# Revit family: Camera-Security-Canon-Box
name_source: partatom
category: Security Devices
revit_build: Autodesk Revit MEP 2012 (Build: 20110916_2132(x64)
units: mm (PartAtom-declared; Revit-internal decimal feet)

## types (4) — shared parameters
Alarm Triggers = External Device Input, Intelligent Function (Video), Intelligent Function (Volume), Timer
Audio In = Φ3.5mm (Φ0.14 in.) Mini-Jack Connector (Monaural), Switch Line IN/MIC IN in the Setting Page. LINE IN x 1 (Connect to an Amplifier Microphone) or MIC IN x 1 (Connect to a Microphone w/o Amplifier)
Date Modified = September 15, 2014
Day and Night = Auto/Manual
Default Elevation = 48 "
Description = See Part Description
Equipment Abbreviation = SC
Family Version = 1.0
IPv4 Protocol = TCP/IP, UDP, HTTP, FTP, SNMP (MIB2), SMTP (Client), DHCP (Client), DNS (Client), ARP, ICMP, POP3, NTP, SMTP Authentication, RTSP, WV-HTTP (Canon Proprietary), ONVIF
Image Sensor = 1/3 type CMOS (Primary Color Filter)
Lens Type = Fixed
Manufacturer = Canon U.S.A., Inc.
Maximum Framerate = JPEG: 0.1 - 30 fps; H.263: 1/2/3/5/6/10/15/30 fps
Minimum Illumination = 0 lx
Model = See Part Number
Model Disclaimer = This 3D model is a simulation of a highly customizable piece of Canon equipment. For assistance in selecting the right Canon equipment for your project, please contact Canon U.S.A., Inc.
Operating Conditions = Temperature:  -10°C - +50°C (+14°F - +122°F); Humidity: 5% - 85% (Without Condensation)
Product Documentation Link = http://www.usa.canon.com
Product Page URL = http://www.usa.canon.com
Scanning System = Progressive
URL = http://www.usa.canon.com
zz Angle 11 = 90.000°
zz Length 10 = 5.118 "
zz Length 14 = -5.96 "
zz Length 19 = 2.28 "
zz Length 20 = 9.71 "
zz Length 23 = 6.529 "
zz Length 26 = 0.157 "
zz Length 28 = 0.736 "
zz Length 3 = 4 "
zz Length 32 = -1.153 "
zz Length 34 = 1.732 "
zz Length 38 = 2.632 "
zz Length 39 = 4.893 "
zz Length 4 = 0.5 "
zz Length 41 = -6.085 "
zz Length 43 = 1.153 "
zz Length 48 = 20 "
zz Length 52 = 2.305 "
zz Length 53 = 3.2 "
zz Length 55 = 0.5 "
zz Length 6 = 6.89 "
zz Length 62 = -1.153 "
zz Length 65 = 1.153 "
zz Length 66 = 8.742 "
zz Length 67 = 6.275 "
zz Length 69 = 6.15 "
zz Length 71 = -6.085 "
zz Length 73 = 1.125 "
zz Length 77 = 3.116 "
zz Length 79 = 6.275 "

## per-type parameters (varying)
| type | Angular Field of View | Effective Pixels | Height | Megapixels | Resolution | Shutter Speed | Width | zz Integer 2 | zz Length 31 | zz Length 36 | zz Length 9 |
| 2.1 MP, Micro | Horizontal: 96° (W) - 96° (T); Vertical: 60.5° (W) - 60.5° (T) | 2.1 Million Pixels | 1.25 " | 2.1 | JPEG, H.264: 1920x1080, 1280x920, 1280x720, 960x5440, 640x480, 640x360, 480x270, 320x240, 320x180 | 1, 1/2, 1/4, 1/8, 1/15, 1/30, 1/60, 1/100, 1/120, 1/250, 1/500, 1/1000, 1/2000, 1/4000, 1/8000, 1/10000, 1/16000 sec. | 2.125 " | 1 | 4.49 " | 2.125 " | 1.25 " |
| 2.1 MP, Standard | Horizontal: 112.6° (W) - 36.7° (T); Vertical: 60.8° (W) - 20.6° (T) | 2.1 Million Pixels | 3.15 " | 2.1 | JPEG, H.264: 1920x1080, 1280x920, 1280x720, 960x5440, 640x480, 640x360, 480x270, 320x240, 320x180 | 1, 1/2, 1/4, 1/8, 1/15, 1/30, 1/60, 1/100, 1/120, 1/250, 1/500, 1/1000, 1/2000, 1/4000, 1/8000, 1/16000 sec. | 2.56 " | 3 | 7.56 " | 2.56 " | 3.15 " |
| 1.3 MP, Standard | Horizontal: 102.5° (W) - 34.2° (T); Vertical: 75.6° (W) – 25.6° (T) | 1.3 Million Pixels | 3.15 " | 1.3 | JPEG, H.264: 1280 x 720, 640 x 360, 320 x 180, 1280 x 960, 640 x 480, 320 x 240 | 1, 1/2, 1/4, 1/8, 1/15, 1/30, 1/60, 1/100, 1/120, 1/250, 1/500, 1/1000, 1/2000, 1/4000, 1/8000, 1/16000 sec. | 2.56 " | 2 | 7.56 " | 2.56 " | 3.15 " |
| 1.3 MP, Micro | Horizontal: 96° (W) - 96° (T); Vertical: 60.5° (W) - 60.5° (T) | 2.1 Million Pixels | 1.25 " | 1.3 | JPEG, H.264: 1280 x 720, 640 x 360, 320 x 180, 1280 x 960, 640 x 480, 320 x 240 | 1, 1/2, 1/4, 1/8, 1/15, 1/30, 1/60, 1/100, 1/120, 1/250, 1/500, 1/1000, 1/2000, 1/4000, 1/8000, 1/10000, 1/16000 sec. | 2.125 " | 4 | 4.49 " | 2.125 " | 1.25 " |

## geometry (parser evidence)
native form markers: Blend x6, Sweep x6
no freeform markers — native parametric forms only
